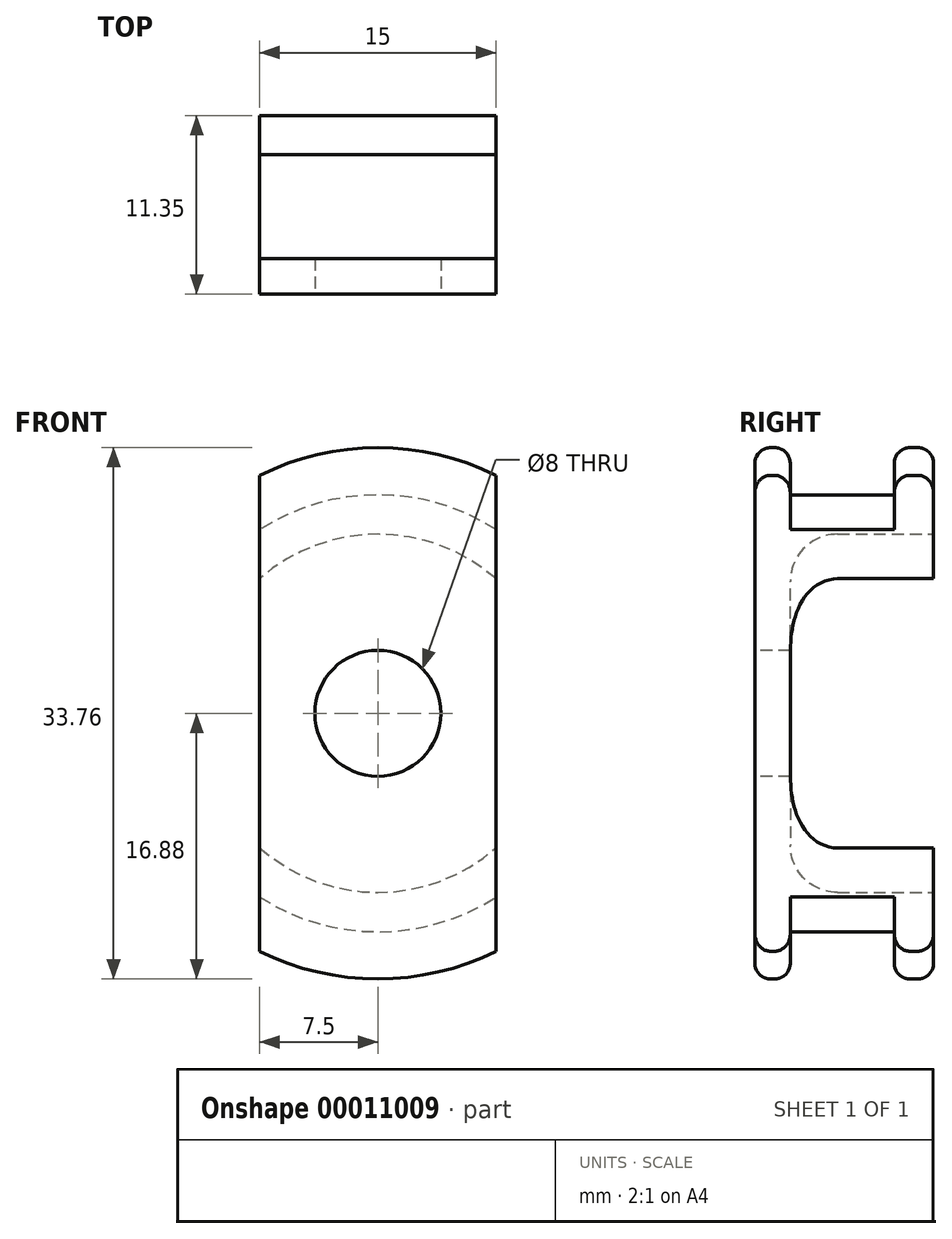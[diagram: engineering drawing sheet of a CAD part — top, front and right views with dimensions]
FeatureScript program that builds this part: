
annotation { "Feature Type Name" : "Feature", "Feature Type Description" : "" }
export const myFeature = defineFeature(function(context is Context, id is Id, definition is map)
    precondition{}
    {
        {
            var Q0;
            Q0=qCreatedBy(makeId("Front.planeOp"),FACE);
            var sketch = newSketch(context, id + "F0", { "sketchPlane" : qUnion([Q0])});
            skCircle(sketch, "E0", {"center": v(0, 0) * mm, "radius": 16.88 * mm});
            skCircle(sketch, "E1.0", {"center": v(0, 0) * mm, "radius": 13.88 * mm});
            skSolve(sketch);
        }
        {
            var Q0;
            Q0=qCreatedBy(makeId("Right.planeOp"),FACE);
            var sketch = newSketch(context, id + "F1", { "sketchPlane" : qUnion([Q0])});
            skLineSegment(sketch, "E2.0", {"start": v(0, -13.88) * mm, "end": v(0, 13.88) * mm, "construction": true});
            skLineSegment(sketch, "E3.0", {"start": v(0, -16.88) * mm, "end": v(0, 16.88) * mm, "construction": true});
            skLineSegment(sketch, "E4.bottom", {"start": v(0, 16.88) * mm, "end": v(-11.35, 16.88) * mm});
            skLineSegment(sketch, "E4.left", {"start": v(0, 16.88) * mm, "end": v(0, 0) * mm});
            skLineSegment(sketch, "E4.right", {"start": v(-11.35, 16.88) * mm, "end": v(-11.35, 0) * mm});
            skLineSegment(sketch, "E5", {"start": v(-2.5, 16.88) * mm, "end": v(-2.5, 0) * mm});
            skLineSegment(sketch, "E6", {"start": v(-9.1, 16.88) * mm, "end": v(-9.1, 0) * mm});
            skLineSegment(sketch, "E7", {"start": v(-9.1, 13.88) * mm, "end": v(-2.5, 13.88) * mm});
            skLineSegment(sketch, "E8", {"start": v(-9.1, 11.38) * mm, "end": v(0, 11.38) * mm});
            skLineSegment(sketch, "E9", {"start": v(0, 0) * mm, "end": v(-11.35, 0) * mm});
            skSolve(sketch);
        }
        {
            var Q0;
            {var subQ3=sQuery(id+"F1.wireOp",EDGE,"E4.left");var subQ6=sQuery(id+"F1.wireOp",EDGE,"E4.bottom");var subQ8=makeQuery(id+"F1.imprint","INTERSECT",VERTEX,{"derivedFrom":[subQ6,subQ3]});Q0=makeQuery(id+"F1.imprint","IMPRINT",FACE,{"disambiguationData":[TD([[makeQuery(id+"F1.imprint","IMPRINT",EDGE,{"disambiguationData":[TD([[subQ8,-1.0]])],"derivedFrom":subQ6}),1.0]])]});}
            var Q1;
            {var subQ5=sQuery(id+"F1.wireOp",EDGE,"E7");Q1=makeQuery(id+"F1.imprint","IMPRINT",FACE,{"disambiguationData":[TD([[makeQuery(id+"F1.imprint","IMPRINT",EDGE,{"derivedFrom":subQ5}),-1.0]])]});}
            var Q2;
            {var subQ7=sQuery(id+"F1.wireOp",EDGE,"E4.right");Q2=makeQuery(id+"F1.imprint","IMPRINT",FACE,{"disambiguationData":[TD([[makeQuery(id+"F1.imprint","IMPRINT",EDGE,{"derivedFrom":subQ7}),1.0]])]});}
            var Q3;
            Q3=sQuery(id+"F1.wireOp",EDGE,"E9");
            revolve(context, id + "F2", {"entities" : qUnion([Q0, Q1, Q2]), "axis" : qUnion([Q3]), "revolveType" : RevolveType.FULL});
        }
        {
            var Q0;
            Q0=makeQuery(id+"F2.opRevolve","SWEPT_FACE",FACE,{"disambiguationData":[OSD([sQuery(id+"F1.wireOp",EDGE,"E4.right")])]});
            var sketch = newSketch(context, id + "F3", { "sketchPlane" : qUnion([Q0])});
            skLineSegment(sketch, "E10.0", {"start": v(0, -16.88) * mm, "end": v(0, 16.88) * mm, "construction": true});
            skLineSegment(sketch, "E11", {"start": v(-7.5, 16.88) * mm, "end": v(7.5, 16.88) * mm, "construction": true});
            skLineSegment(sketch, "E12.rect.bottom", {"start": v(7.5, 16.88) * mm, "end": v(-7.5, 16.88) * mm});
            skLineSegment(sketch, "E12.rect.top", {"start": v(7.5, -16.88) * mm, "end": v(-7.5, -16.88) * mm});
            skLineSegment(sketch, "E12.rect.left", {"start": v(7.5, 16.88) * mm, "end": v(7.5, -16.88) * mm});
            skLineSegment(sketch, "E12.rect.right", {"start": v(-7.5, 16.88) * mm, "end": v(-7.5, -16.88) * mm});
            skPoint(sketch, "E12.rect.middle", {"position": v(0, 0) * mm});
            skCircle(sketch, "E13", {"center": v(0, 0) * mm, "radius": 4 * mm});
            skCircle(sketch, "E14", {"center": v(0, 0) * mm, "radius": 5.5 * mm});
            skLineSegment(sketch, "E15", {"start": v(-5.5, 0) * mm, "end": v(-7.5, 0) * mm});
            skSolve(sketch);
        }
        {
            var Q0;
            Q0=makeQuery(id+"F2.opRevolve","SWEPT_EDGE",EDGE,{"disambiguationData":[OSD([sQuery(id+"F1.wireOp",EDGE,"E4.bottom"),sQuery(id+"F1.wireOp",EDGE,"E4.left")])]});
            var Q1;
            Q1=makeQuery(id+"F2.opRevolve","SWEPT_EDGE",EDGE,{"disambiguationData":[OSD([sQuery(id+"F1.wireOp",EDGE,"E4.bottom"),sQuery(id+"F1.wireOp",EDGE,"E5")])]});
            var Q2;
            Q2=makeQuery(id+"F2.opRevolve","SWEPT_EDGE",EDGE,{"disambiguationData":[OSD([sQuery(id+"F1.wireOp",EDGE,"E4.bottom"),sQuery(id+"F1.wireOp",EDGE,"E6")])]});
            var Q3;
            Q3=makeQuery(id+"F2.opRevolve","SWEPT_EDGE",EDGE,{"disambiguationData":[OSD([sQuery(id+"F1.wireOp",EDGE,"E4.bottom"),sQuery(id+"F1.wireOp",EDGE,"E4.right")])]});
            fillet(context, id + "F4", {"entities" : qUnion([Q0, Q1, Q2, Q3]), "radius" : 1 * mm, "tangentPropagation" : true, "allowEdgeOverflow" : false});
        }
        {
            var Q0;
            Q0=makeQuery(id+"F2.opRevolve","SWEPT_EDGE",EDGE,{"disambiguationData":[OSD([sQuery(id+"F1.wireOp",EDGE,"E6"),sQuery(id+"F1.wireOp",EDGE,"E8")])]});
            fillet(context, id + "F5", {"entities" : qUnion([Q0]), "radius" : 3 * mm, "tangentPropagation" : true, "allowEdgeOverflow" : false});
        }
        {
            var Q0;
            {var subQ0=makeQuery(id+"F2.opRevolve","SWEPT_EDGE",EDGE,{"disambiguationData":[OSD([sQuery(id+"F1.wireOp",EDGE,"E4.bottom"),sQuery(id+"F1.wireOp",EDGE,"E4.right")])]});var subQ4=sQuery(id+"F3.wireOp",EDGE,"E12.rect.left");var subQ8=makeQuery(id+"F3.imprint","INTERSECT",VERTEX,{"disambiguationData":[OD(0.0)],"derivedFrom":[subQ0,subQ4]});Q0=makeQuery(id+"F3.imprint","IMPRINT",FACE,{"disambiguationData":[TD([[makeQuery(id+"F3.imprint","IMPRINT",EDGE,{"disambiguationData":[TD([[subQ8,-1.0]])],"derivedFrom":subQ4}),-1.0]])]});}
            var Q1;
            Q1=makeQuery(id+"F3.imprint","IMPRINT",FACE,{"disambiguationData":[TD([[makeQuery(id+"F3.imprint","IMPRINT",EDGE,{"derivedFrom":sQuery(id+"F3.wireOp",EDGE,"E13")}),-1.0]])]});
            var Q2;
            Q2=makeQuery(id+"F3.imprint","IMPRINT",FACE,{"disambiguationData":[TD([[makeQuery(id+"F3.imprint","IMPRINT",EDGE,{"derivedFrom":sQuery(id+"F3.wireOp",EDGE,"E14")}),-1.0]])]});
            extrude(context, id + "F6", {"entities" : qUnion([Q0, Q1, Q2]), "operationType" : NewBodyOperationType.INTERSECT, "endBound" : BoundingType.THROUGH_ALL, "oppositeDirection" : true, "depth" : 25 * mm});
        }
    });
